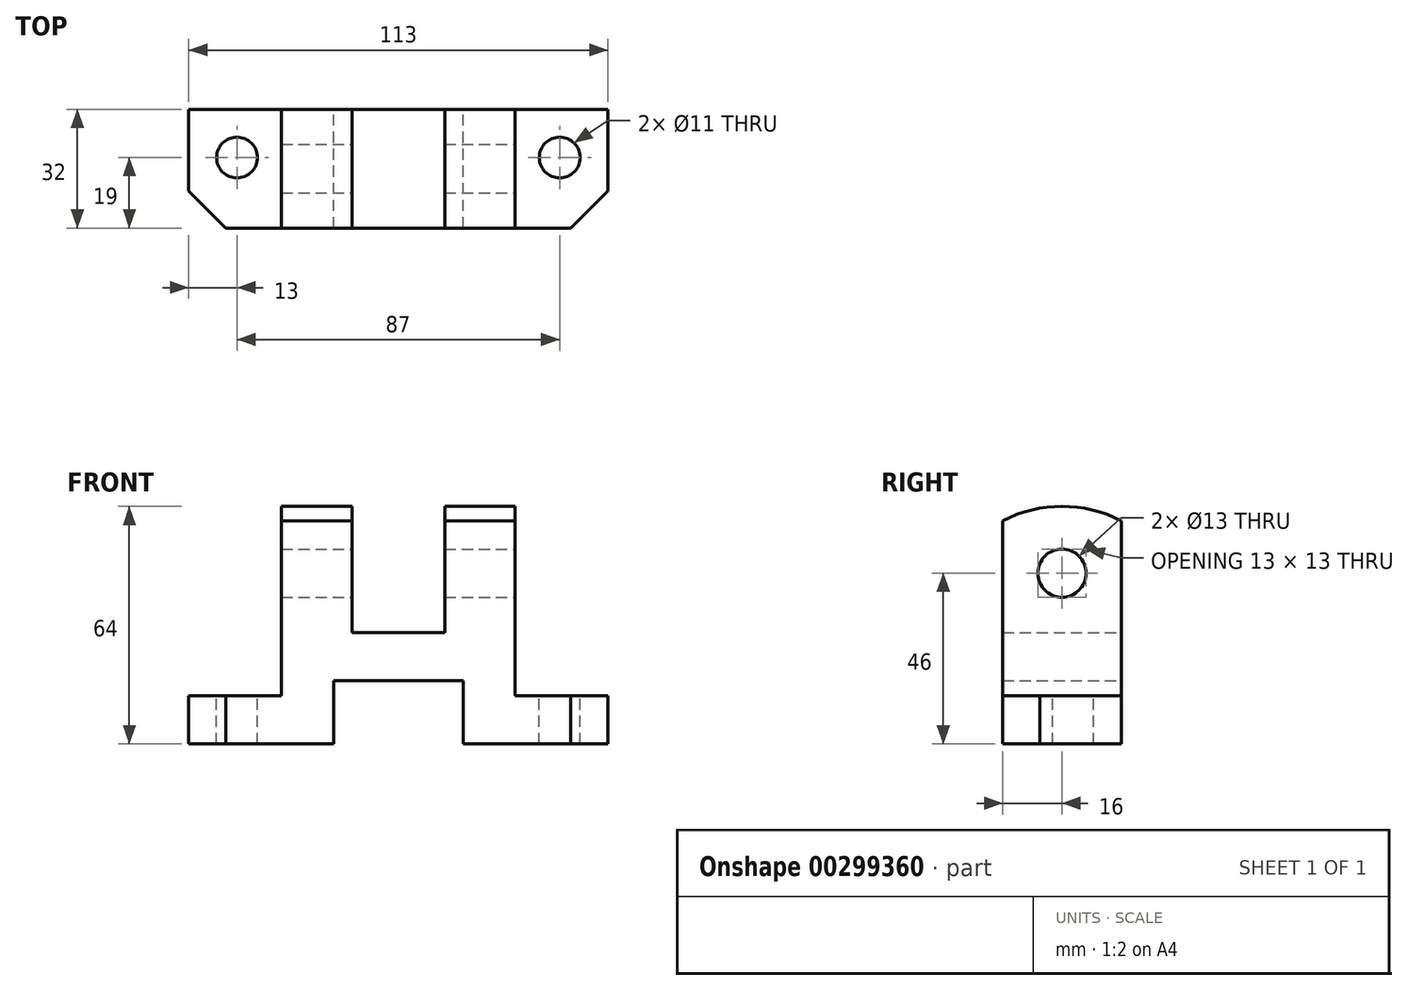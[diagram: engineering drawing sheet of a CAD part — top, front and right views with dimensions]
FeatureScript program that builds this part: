
annotation { "Feature Type Name" : "Feature", "Feature Type Description" : "" }
export const myFeature = defineFeature(function(context is Context, id is Id, definition is map)
    precondition{}
    {
        {
            var Q0;
            Q0=qCreatedBy(makeId("Front.planeOp"),FACE);
            var sketch = newSketch(context, id + "F0", { "sketchPlane" : qUnion([Q0])});
            skLineSegment(sketch, "E0", {"start": v(0, 6.5) * mm, "end": v(12.5, 6.5) * mm});
            skLineSegment(sketch, "E1", {"start": v(12.5, 6.5) * mm, "end": v(12.5, 40.5) * mm});
            skLineSegment(sketch, "E2", {"start": v(12.5, 40.5) * mm, "end": v(31.5, 40.5) * mm});
            skLineSegment(sketch, "E3", {"start": v(31.5, 40.5) * mm, "end": v(31.5, -10.5) * mm});
            skLineSegment(sketch, "E4", {"start": v(31.5, -10.5) * mm, "end": v(56.5, -10.5) * mm});
            skLineSegment(sketch, "E5", {"start": v(56.5, -10.5) * mm, "end": v(56.5, -23.5) * mm});
            skLineSegment(sketch, "E6", {"start": v(56.5, -23.5) * mm, "end": v(17.5, -23.5) * mm});
            skLineSegment(sketch, "E7", {"start": v(17.5, -23.5) * mm, "end": v(17.5, -6.5) * mm});
            skLineSegment(sketch, "E8", {"start": v(17.5, -6.5) * mm, "end": v(0, -6.5) * mm});
            skLineSegment(sketch, "E9", {"start": v(0, 42.26) * mm, "end": v(0, -42.26) * mm, "construction": true});
            skLineSegment(sketch, "E10.MirrorCS", {"start": v(0, 6.5) * mm, "end": v(-12.5, 6.5) * mm});
            skLineSegment(sketch, "E11.MirrorCS", {"start": v(-12.5, 6.5) * mm, "end": v(-12.5, 40.5) * mm});
            skLineSegment(sketch, "E12.MirrorCS", {"start": v(-31.5, 40.5) * mm, "end": v(-31.5, -10.5) * mm});
            skLineSegment(sketch, "E13.MirrorCS", {"start": v(-12.5, 40.5) * mm, "end": v(-31.5, 40.5) * mm});
            skLineSegment(sketch, "E14.MirrorCS", {"start": v(-56.5, -23.5) * mm, "end": v(-17.5, -23.5) * mm});
            skLineSegment(sketch, "E15.MirrorCS", {"start": v(-31.5, -10.5) * mm, "end": v(-56.5, -10.5) * mm});
            skLineSegment(sketch, "E16.MirrorCS", {"start": v(-56.5, -10.5) * mm, "end": v(-56.5, -23.5) * mm});
            skLineSegment(sketch, "E17.MirrorCS", {"start": v(-17.5, -6.5) * mm, "end": v(0, -6.5) * mm});
            skLineSegment(sketch, "E18.MirrorCS", {"start": v(-17.5, -23.5) * mm, "end": v(-17.5, -6.5) * mm});
            skSolve(sketch);
        }
        {
            var Q0;
            Q0 = qSketchRegion(id + "F0", true);
            extrude(context, id + "F1", {"entities" : qUnion([Q0]), "endBound" : BoundingType.SYMMETRIC, "depth" : 32 * mm});
        }
        {
            var Q0;
            Q0=qCreatedBy(makeId("Top.planeOp"),FACE);
            var sketch = newSketch(context, id + "F2", { "sketchPlane" : qUnion([Q0])});
            skLineSegment(sketch, "E19", {"start": v(-56.5, -6) * mm, "end": v(-56.5, -16) * mm});
            skLineSegment(sketch, "E20", {"start": v(-56.5, -16) * mm, "end": v(-46.5, -16) * mm});
            skLineSegment(sketch, "E21", {"start": v(-46.5, -16) * mm, "end": v(-56.5, -6) * mm});
            skLineSegment(sketch, "E22.MirrorCS", {"start": v(56.5, -6) * mm, "end": v(56.5, -16) * mm});
            skLineSegment(sketch, "E23.MirrorCS", {"start": v(46.5, -16) * mm, "end": v(56.5, -6) * mm});
            skLineSegment(sketch, "E24.MirrorCS", {"start": v(56.5, -16) * mm, "end": v(46.5, -16) * mm});
            skSolve(sketch);
        }
        {
            var Q0;
            Q0 = qSketchRegion(id + "F2", true);
            extrude(context, id + "F3", {"entities" : qUnion([Q0]), "operationType" : NewBodyOperationType.REMOVE, "endBound" : BoundingType.THROUGH_ALL, "oppositeDirection" : true, "depth" : 25 * mm});
        }
        {
            var Q0;
            Q0=qCreatedBy(makeId("Top.planeOp"),FACE);
            var sketch = newSketch(context, id + "F4", { "sketchPlane" : qUnion([Q0])});
            skCircle(sketch, "E25", {"center": v(43.5, 3) * mm, "radius": 5.5 * mm});
            skCircle(sketch, "E26.MirrorC", {"center": v(-43.5, 3) * mm, "radius": 5.5 * mm});
            skSolve(sketch);
        }
        {
            var Q0;
            Q0 = qSketchRegion(id + "F4", true);
            extrude(context, id + "F5", {"entities" : qUnion([Q0]), "operationType" : NewBodyOperationType.REMOVE, "endBound" : BoundingType.THROUGH_ALL, "oppositeDirection" : true, "depth" : 25 * mm});
        }
        {
            var Q0;
            Q0=makeQuery(id+"F1.opExtrude","SWEPT_FACE",FACE,{"disambiguationData":[OSD([sQuery(id+"F0.wireOp",EDGE,"E3")])]});
            var sketch = newSketch(context, id + "F6", { "sketchPlane" : qUnion([Q0])});
            skCircle(sketch, "E27", {"center": v(0, 22.5) * mm, "radius": 6.5 * mm});
            skArc(sketch, "E28", {"start": v(16, 36.63) * mm, "mid": v(0, 40.5) * mm, "end": v(-16, 36.63) * mm});
            skSolve(sketch);
        }
        {
            var Q0;
            {var subQ0=sQuery(id+"F6.wireOp",EDGE,"E28");var subQ1=sQuery(id+"F0.wireOp",EDGE,"E3");var subQ2=makeQuery(id+"F1.opExtrude","CAP_EDGE",EDGE,{"disambiguationData":[OSD([subQ1])],"isStart":false});var subQ3=makeQuery(id+"F6.imprint","INTERSECT",VERTEX,{"derivedFrom":[subQ2,subQ0]});Q0=makeQuery(id+"F6.imprint","IMPRINT",FACE,{"disambiguationData":[TD([[makeQuery(id+"F6.imprint","IMPRINT",EDGE,{"disambiguationData":[TD([[subQ3,1.0]])],"derivedFrom":subQ0}),-1.0]])]});}
            var Q1;
            {var subQ0=sQuery(id+"F6.wireOp",EDGE,"E28");var subQ1=sQuery(id+"F0.wireOp",EDGE,"E3");var subQ2=makeQuery(id+"F1.opExtrude","CAP_EDGE",EDGE,{"disambiguationData":[OSD([subQ1])],"isStart":true});var subQ3=makeQuery(id+"F6.imprint","INTERSECT",VERTEX,{"derivedFrom":[subQ2,subQ0]});Q1=makeQuery(id+"F6.imprint","IMPRINT",FACE,{"disambiguationData":[TD([[makeQuery(id+"F6.imprint","IMPRINT",EDGE,{"disambiguationData":[TD([[subQ3,-1.0]])],"derivedFrom":subQ0}),-1.0]])]});}
            extrude(context, id + "F7", {"entities" : qUnion([Q0, Q1]), "operationType" : NewBodyOperationType.REMOVE, "endBound" : BoundingType.THROUGH_ALL, "oppositeDirection" : true, "depth" : 25 * mm});
        }
        {
            var Q0;
            Q0=makeQuery(id+"F6.imprint","IMPRINT",FACE,{"disambiguationData":[TD([[makeQuery(id+"F6.imprint","IMPRINT",EDGE,{"derivedFrom":sQuery(id+"F6.wireOp",EDGE,"E27")}),1.0]])]});
            extrude(context, id + "F8", {"entities" : qUnion([Q0]), "operationType" : NewBodyOperationType.REMOVE, "endBound" : BoundingType.THROUGH_ALL, "oppositeDirection" : true, "depth" : 25 * mm});
        }
    });
